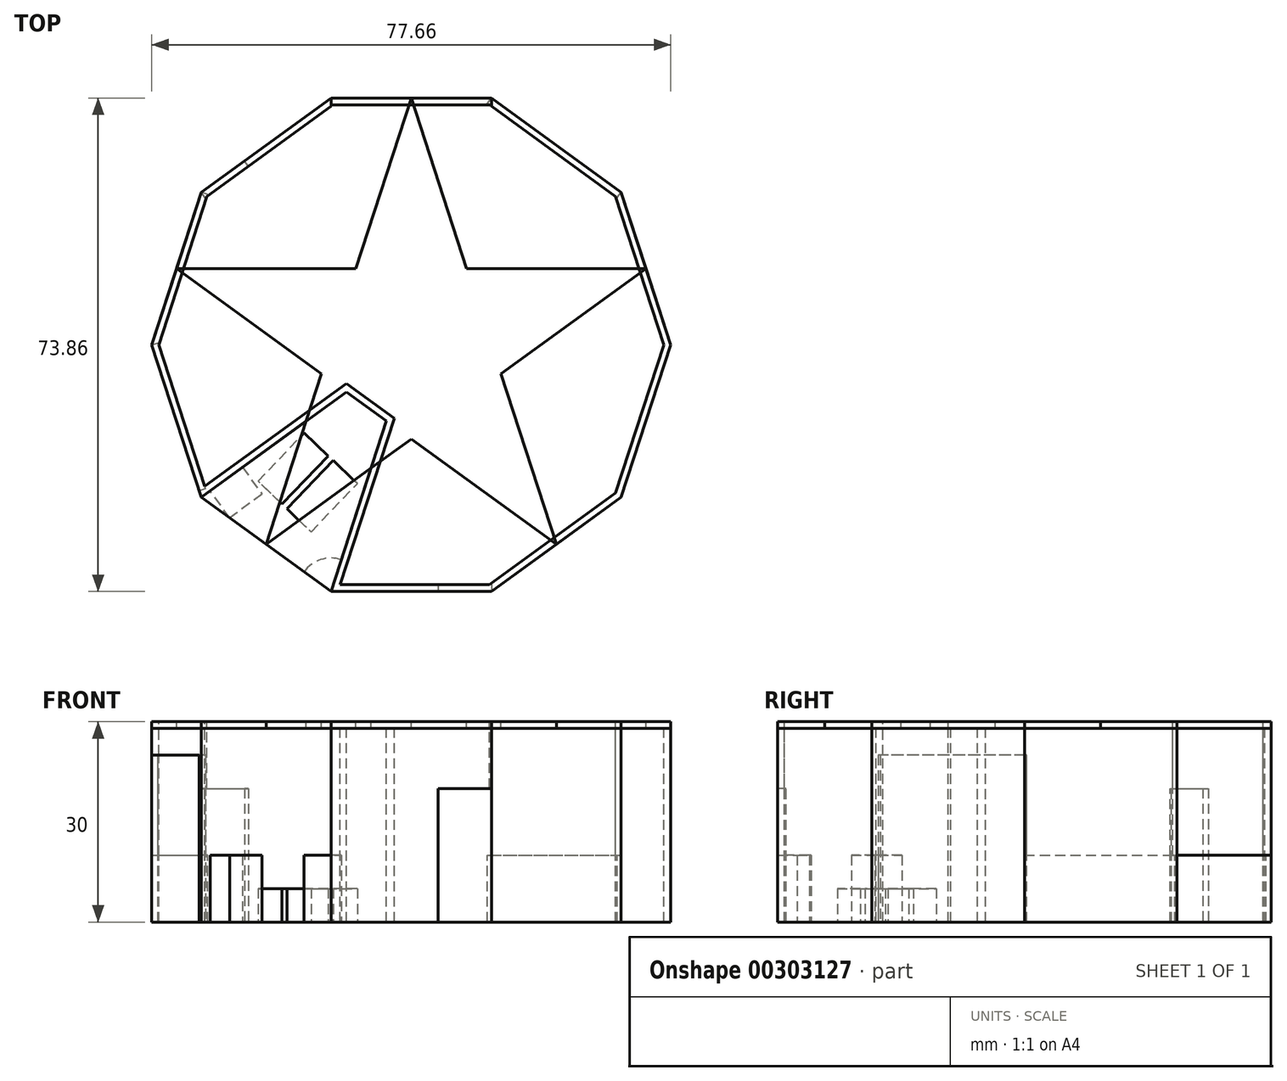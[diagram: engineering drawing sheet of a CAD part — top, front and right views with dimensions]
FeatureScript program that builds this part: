
annotation { "Feature Type Name" : "Feature", "Feature Type Description" : "" }
export const myFeature = defineFeature(function(context is Context, id is Id, definition is map)
    precondition{}
    {
        {
            var Q0;
            Q0=qCreatedBy(makeId("Top.planeOp"),FACE);
            var sketch = newSketch(context, id + "F0", { "sketchPlane" : qUnion([Q0])});
            skCircle(sketch, "E0.cCircle", {"center": v(0, 0) * mm, "radius": 38.83 * mm, "construction": true});
            skLineSegment(sketch, "E0.0", {"start": v(12, 36.93) * mm, "end": v(31.42, 22.83) * mm});
            skLineSegment(sketch, "E0.1", {"start": v(31.42, 22.83) * mm, "end": v(38.83, 0) * mm});
            skLineSegment(sketch, "E0.2", {"start": v(38.83, 0) * mm, "end": v(31.42, -22.83) * mm});
            skLineSegment(sketch, "E0.3", {"start": v(31.42, -22.83) * mm, "end": v(12, -36.93) * mm});
            skLineSegment(sketch, "E0.4", {"start": v(12, -36.93) * mm, "end": v(-12, -36.93) * mm});
            skLineSegment(sketch, "E0.5", {"start": v(-12, -36.93) * mm, "end": v(-31.42, -22.83) * mm});
            skLineSegment(sketch, "E0.6", {"start": v(-31.42, -22.83) * mm, "end": v(-38.83, 0) * mm});
            skLineSegment(sketch, "E0.7", {"start": v(-38.83, 0) * mm, "end": v(-31.42, 22.83) * mm});
            skLineSegment(sketch, "E0.8", {"start": v(-31.42, 22.83) * mm, "end": v(-12, 36.93) * mm});
            skLineSegment(sketch, "E0.9", {"start": v(-12, 36.93) * mm, "end": v(12, 36.93) * mm});
            skSolve(sketch);
        }
        {
            var Q0;
            Q0=makeQuery(id+"F0.imprint","IMPRINT",FACE,{"disambiguationData":[TD([[makeQuery(id+"F0.imprint","IMPRINT",EDGE,{"derivedFrom":sQuery(id+"F0.wireOp",EDGE,"E0.0")}),-1.0]])]});
            extrude(context, id + "F1", {"entities" : qUnion([Q0]), "oppositeDirection" : true, "depth" : 30 * mm});
        }
        {
            var Q0;
            Q0 = qSketchRegion(id + "F0", true);
            var sketch = newSketch(context, id + "F2", { "sketchPlane" : qUnion([Q0])});
            skLineSegment(sketch, "E1", {"start": v(0, 36.93) * mm, "end": v(-21.7, -29.88) * mm});
            skLineSegment(sketch, "E2", {"start": v(-21.7, -29.88) * mm, "end": v(35.12, 11.41) * mm});
            skLineSegment(sketch, "E3", {"start": v(35.12, 11.41) * mm, "end": v(-35.12, 11.41) * mm});
            skLineSegment(sketch, "E4", {"start": v(-35.12, 11.41) * mm, "end": v(21.7, -29.88) * mm});
            skLineSegment(sketch, "E5", {"start": v(21.7, -29.88) * mm, "end": v(0, 36.93) * mm});
            skSolve(sketch);
        }
        {
            var Q0;
            Q0 = qSketchRegion(id + "F0", true);
            var sketch = newSketch(context, id + "F3", { "sketchPlane" : qUnion([Q0])});
            skLineSegment(sketch, "E6", {"start": v(-31.42, -22.83) * mm, "end": v(0, 0) * mm});
            skLineSegment(sketch, "E7", {"start": v(0, 0) * mm, "end": v(-12, -36.93) * mm});
            skLineSegment(sketch, "E8", {"start": v(-12, -36.93) * mm, "end": v(-31.42, -22.83) * mm});
            skSolve(sketch);
        }
        {
            var Q0;
            Q0 = qSketchRegion(id + "F3", true);
            extrude(context, id + "F4", {"entities" : qUnion([Q0]), "operationType" : NewBodyOperationType.REMOVE, "oppositeDirection" : true, "depth" : 30 * mm});
        }
        {
            var Q0;
            Q0=makeQuery(id+"F1.opExtrude","CAP_FACE",FACE,{"disambiguationData":[OSD([sQuery(id+"F0.wireOp",EDGE,"E0.0"),sQuery(id+"F0.wireOp",EDGE,"E0.1"),sQuery(id+"F0.wireOp",EDGE,"E0.2"),sQuery(id+"F0.wireOp",EDGE,"E0.3"),sQuery(id+"F0.wireOp",EDGE,"E0.4"),sQuery(id+"F0.wireOp",EDGE,"E0.5"),sQuery(id+"F0.wireOp",EDGE,"E0.6"),sQuery(id+"F0.wireOp",EDGE,"E0.7"),sQuery(id+"F0.wireOp",EDGE,"E0.8"),sQuery(id+"F0.wireOp",EDGE,"E0.9")])],"isStart":false});
            var sketch = newSketch(context, id + "F5", { "sketchPlane" : qUnion([Q0])});
            skLineSegment(sketch, "E9", {"start": v(-31.42, 22.83) * mm, "end": v(-12, 36.93) * mm, "construction": true});
            skLineSegment(sketch, "E10", {"start": v(-30.1, 21.87) * mm, "end": v(-25.25, 18.34) * mm});
            skLineSegment(sketch, "E11", {"start": v(-25.25, 18.34) * mm, "end": v(-22.3, 22.39) * mm});
            skLineSegment(sketch, "E12", {"start": v(-22.3, 22.39) * mm, "end": v(-27.16, 25.92) * mm});
            skLineSegment(sketch, "E13", {"start": v(-27.16, 25.92) * mm, "end": v(-30.1, 21.87) * mm});
            skLineSegment(sketch, "E14", {"start": v(-31.42, 22.83) * mm, "end": v(-38.83, 0) * mm});
            skLineSegment(sketch, "E15", {"start": v(-38.83, 0) * mm, "end": v(-31.42, -22.83) * mm});
            skLineSegment(sketch, "E16", {"start": v(-31.42, -22.83) * mm, "end": v(-24.94, -27.53) * mm});
            skLineSegment(sketch, "E17", {"start": v(-12, -36.93) * mm, "end": v(12, -36.93) * mm});
            skLineSegment(sketch, "E18", {"start": v(12, -36.93) * mm, "end": v(31.42, -22.83) * mm});
            skPoint(sketch, "E19.endSnap0", {"position": v(-6, 18.47) * mm});
            skArc(sketch, "E20", {"start": v(-16.05, 34) * mm, "mid": v(-13.55, 32.18) * mm, "end": v(-10.45, 32.18) * mm});
            skLineSegment(sketch, "E21", {"start": v(12, 36.93) * mm, "end": v(4, 36.93) * mm});
            skLineSegment(sketch, "E22", {"start": v(-12, 36.93) * mm, "end": v(-16.05, 34) * mm});
            skLineSegment(sketch, "E23", {"start": v(-10.45, 32.18) * mm, "end": v(-12, 36.93) * mm});
            skLineSegment(sketch, "E24", {"start": v(-22.93, 20.41) * mm, "end": v(-16.02, 13.18) * mm});
            skLineSegment(sketch, "E25", {"start": v(-16.02, 13.18) * mm, "end": v(-12.4, 16.64) * mm});
            skLineSegment(sketch, "E26", {"start": v(-12.4, 16.64) * mm, "end": v(-19.31, 23.87) * mm});
            skLineSegment(sketch, "E27", {"start": v(-19.31, 23.87) * mm, "end": v(-22.93, 20.41) * mm});
            skLineSegment(sketch, "E28", {"start": v(-8.07, 20.78) * mm, "end": v(-11.68, 17.33) * mm});
            skLineSegment(sketch, "E29", {"start": v(-18.6, 24.56) * mm, "end": v(-14.98, 28.01) * mm});
            skLineSegment(sketch, "E30", {"start": v(-14.98, 28.01) * mm, "end": v(-8.07, 20.78) * mm});
            skLineSegment(sketch, "E31", {"start": v(-18.6, 24.56) * mm, "end": v(-11.68, 17.33) * mm});
            skLineSegment(sketch, "E32", {"start": v(-19.31, 23.87) * mm, "end": v(-18.6, 24.56) * mm, "construction": true});
            skLineSegment(sketch, "E33", {"start": v(-12.4, 16.64) * mm, "end": v(-11.68, 17.33) * mm, "construction": true});
            skSolve(sketch);
        }
        {
            var Q0;
            Q0=makeQuery(id+"F5.imprint","IMPRINT",FACE,{"disambiguationData":[TD([[makeQuery(id+"F5.imprint","IMPRINT",EDGE,{"derivedFrom":sQuery(id+"F5.wireOp",EDGE,"E20")}),1.0]])]});
            extrude(context, id + "F6", {"entities" : qUnion([Q0]), "oppositeDirection" : true, "depth" : 10 * mm});
        }
        {
            var Q0;
            Q0=makeQuery(id+"F5.imprint","IMPRINT",FACE,{"disambiguationData":[TD([[makeQuery(id+"F5.imprint","IMPRINT",EDGE,{"derivedFrom":sQuery(id+"F5.wireOp",EDGE,"E24")}),1.0]])]});
            var Q1;
            Q1=makeQuery(id+"F5.imprint","IMPRINT",FACE,{"disambiguationData":[TD([[makeQuery(id+"F5.imprint","IMPRINT",EDGE,{"derivedFrom":sQuery(id+"F5.wireOp",EDGE,"E28")}),-1.0]])]});
            extrude(context, id + "F7", {"entities" : qUnion([Q0, Q1]), "oppositeDirection" : true, "depth" : 5 * mm});
        }
        {
            var Q0;
            {var subQ1=sQuery(id+"F2.wireOp",EDGE,"E1");var subQ3=sQuery(id+"F2.wireOp",EDGE,"E4");var subQ4=makeQuery(id+"F2.imprint","INTERSECT",VERTEX,{"derivedFrom":[subQ1,subQ3]});Q0=makeQuery(id+"F2.imprint","IMPRINT",FACE,{"disambiguationData":[TD([[makeQuery(id+"F2.imprint","IMPRINT",EDGE,{"disambiguationData":[TD([[subQ4,-1.0]])],"derivedFrom":subQ3}),-1.0]])]});}
            var sketch = newSketch(context, id + "F8", { "sketchPlane" : qUnion([Q0])});
            skLineSegment(sketch, "E34", {"start": v(0, 0) * mm, "end": v(-3.7, -11.41) * mm});
            skLineSegment(sketch, "E35", {"start": v(-3.7, -11.41) * mm, "end": v(-9.7, -7.05) * mm});
            skLineSegment(sketch, "E36", {"start": v(-9.7, -7.05) * mm, "end": v(0, 0) * mm});
            skSolve(sketch);
        }
        {
            var Q0;
            Q0 = qSketchRegion(id + "F8", true);
            extrude(context, id + "F9", {"entities" : qUnion([Q0]), "operationType" : NewBodyOperationType.ADD, "oppositeDirection" : true, "depth" : 30 * mm});
        }
        {
            var Q0;
            Q0=makeQuery(id+"F9.boolean.opBoolean","MERGE",FACE,{"derivedFrom":[makeQuery(id+"FY8pf64QO3TvRso_1.boolean.opBoolean","MERGE",FACE,{"derivedFrom":[makeQuery(id+"F1.opExtrude","CAP_FACE",FACE,{"disambiguationData":[OSD([sQuery(id+"F0.wireOp",EDGE,"E0.0"),sQuery(id+"F0.wireOp",EDGE,"E0.1"),sQuery(id+"F0.wireOp",EDGE,"E0.2"),sQuery(id+"F0.wireOp",EDGE,"E0.3"),sQuery(id+"F0.wireOp",EDGE,"E0.4"),sQuery(id+"F0.wireOp",EDGE,"E0.5"),sQuery(id+"F0.wireOp",EDGE,"E0.6"),sQuery(id+"F0.wireOp",EDGE,"E0.7"),sQuery(id+"F0.wireOp",EDGE,"E0.8"),sQuery(id+"F0.wireOp",EDGE,"E0.9")])],"isStart":false}),makeQuery(id+"FY8pf64QO3TvRso_1.opExtrude","CAP_FACE",FACE,{"disambiguationData":[OSD([sQuery(id+"F5.wireOp",EDGE,"E10"),sQuery(id+"F5.wireOp",EDGE,"E11"),sQuery(id+"F5.wireOp",EDGE,"E12"),sQuery(id+"F5.wireOp",EDGE,"E13")])],"isStart":true})]}),makeQuery(id+"F9.opExtrude","CAP_FACE",FACE,{"disambiguationData":[OSD([sQuery(id+"F8.wireOp",EDGE,"E34"),sQuery(id+"F8.wireOp",EDGE,"E35"),sQuery(id+"F8.wireOp",EDGE,"E36")])],"isStart":false})]});
            var Q1;
            Q1=makeQuery(id+"F9.boolean.opBoolean","MERGE",FACE,{"derivedFrom":[makeQuery(id+"F1.opExtrude","CAP_FACE",FACE,{"disambiguationData":[OSD([sQuery(id+"F0.wireOp",EDGE,"E0.0"),sQuery(id+"F0.wireOp",EDGE,"E0.1"),sQuery(id+"F0.wireOp",EDGE,"E0.2"),sQuery(id+"F0.wireOp",EDGE,"E0.3"),sQuery(id+"F0.wireOp",EDGE,"E0.4"),sQuery(id+"F0.wireOp",EDGE,"E0.5"),sQuery(id+"F0.wireOp",EDGE,"E0.6"),sQuery(id+"F0.wireOp",EDGE,"E0.7"),sQuery(id+"F0.wireOp",EDGE,"E0.8"),sQuery(id+"F0.wireOp",EDGE,"E0.9")])],"isStart":true}),makeQuery(id+"F9.opExtrude","CAP_FACE",FACE,{"disambiguationData":[OSD([sQuery(id+"F8.wireOp",EDGE,"E34"),sQuery(id+"F8.wireOp",EDGE,"E35"),sQuery(id+"F8.wireOp",EDGE,"E36")])],"isStart":true})]});
            shell(context, id + "F10", {"entities" : qUnion([Q0, Q1]), "thickness" : 1 * mm});
        }
        {
            var Q0;
            Q0=makeQuery(id+"F1.opExtrude","SWEPT_FACE",FACE,{"disambiguationData":[OSD([sQuery(id+"F0.wireOp",EDGE,"E0.4")])]});
            var sketch = newSketch(context, id + "F11", { "sketchPlane" : qUnion([Q0])});
            skLineSegment(sketch, "E37", {"start": v(4, -30) * mm, "end": v(4, -10) * mm});
            skLineSegment(sketch, "E38", {"start": v(4, -10) * mm, "end": v(12, -10) * mm});
            skLineSegment(sketch, "E39", {"start": v(12, -10) * mm, "end": v(12, -30) * mm});
            skLineSegment(sketch, "E40", {"start": v(12, -30) * mm, "end": v(4, -30) * mm});
            skSolve(sketch);
        }
        {
            var Q0;
            Q0=makeQuery(id+"F11.imprint","IMPRINT",FACE,{"disambiguationData":[TD([[makeQuery(id+"F11.imprint","IMPRINT",EDGE,{"derivedFrom":sQuery(id+"F11.wireOp",EDGE,"E37")}),-1.0]])]});
            extrude(context, id + "F12", {"entities" : qUnion([Q0]), "operationType" : NewBodyOperationType.REMOVE, "endBound" : BoundingType.UP_TO_NEXT, "oppositeDirection" : true, "depth" : 25 * mm});
        }
        {
            var Q0;
            Q0=makeQuery(id+"F1.opExtrude","SWEPT_FACE",FACE,{"disambiguationData":[OSD([sQuery(id+"F0.wireOp",EDGE,"E0.7")])]});
            var sketch = newSketch(context, id + "F13", { "sketchPlane" : qUnion([Q0])});
            skLineSegment(sketch, "E41", {"start": v(-12, -30) * mm, "end": v(12, -30) * mm});
            skLineSegment(sketch, "E42", {"start": v(12, -30) * mm, "end": v(12, -20) * mm});
            skLineSegment(sketch, "E43", {"start": v(12, -20) * mm, "end": v(-12, -20) * mm});
            skLineSegment(sketch, "E44", {"start": v(-12, -20) * mm, "end": v(-12, -30) * mm});
            skSolve(sketch);
        }
        {
            var Q0;
            Q0=makeQuery(id+"F13.imprint","IMPRINT",FACE,{"disambiguationData":[TD([[makeQuery(id+"F13.imprint","IMPRINT",EDGE,{"derivedFrom":sQuery(id+"F13.wireOp",EDGE,"E41")}),-1.0]])]});
            extrude(context, id + "F14", {"entities" : qUnion([Q0]), "operationType" : NewBodyOperationType.REMOVE, "endBound" : BoundingType.UP_TO_NEXT, "oppositeDirection" : true, "depth" : 25 * mm});
        }
        {
            var Q0;
            Q0=makeQuery(id+"F13.imprint","IMPRINT",FACE,{"disambiguationData":[TD([[makeQuery(id+"F13.imprint","IMPRINT",EDGE,{"derivedFrom":sQuery(id+"F13.wireOp",EDGE,"E41")}),-1.0]])]});
            extrude(context, id + "F15", {"entities" : qUnion([Q0]), "oppositeDirection" : true, "depth" : 1 * mm});
        }
        {
            var Q0;
            Q0=makeQuery(id+"F1.opExtrude","SWEPT_FACE",FACE,{"disambiguationData":[OSD([sQuery(id+"F0.wireOp",EDGE,"E0.8")])]});
            var sketch = newSketch(context, id + "F16", { "sketchPlane" : qUnion([Q0])});
            skLineSegment(sketch, "E45", {"start": v(12, -30) * mm, "end": v(12, -10) * mm});
            skLineSegment(sketch, "E46", {"start": v(12, -10) * mm, "end": v(4, -10) * mm});
            skLineSegment(sketch, "E47", {"start": v(4, -10) * mm, "end": v(4, -30) * mm});
            skLineSegment(sketch, "E48", {"start": v(4, -30) * mm, "end": v(12, -30) * mm});
            skSolve(sketch);
        }
        {
            var Q0;
            {var subQ0=sQuery(id+"F16.wireOp",EDGE,"E46");Q0=makeQuery(id+"F16.imprint","IMPRINT",FACE,{"disambiguationData":[TD([[makeQuery(id+"F16.imprint","IMPRINT",EDGE,{"derivedFrom":subQ0}),1.0]])]});}
            extrude(context, id + "F17", {"entities" : qUnion([Q0]), "operationType" : NewBodyOperationType.REMOVE, "endBound" : BoundingType.UP_TO_NEXT, "oppositeDirection" : true, "depth" : 25 * mm});
        }
        {
            var Q0;
            {var subQ0=sQuery(id+"F16.wireOp",EDGE,"E46");Q0=makeQuery(id+"F16.imprint","IMPRINT",FACE,{"disambiguationData":[TD([[makeQuery(id+"F16.imprint","IMPRINT",EDGE,{"derivedFrom":subQ0}),1.0]])]});}
            extrude(context, id + "F18", {"entities" : qUnion([Q0]), "oppositeDirection" : true, "depth" : 1 * mm});
        }
        {
            var Q0;
            Q0=makeQuery(id+"F1.opExtrude","SWEPT_FACE",FACE,{"disambiguationData":[OSD([sQuery(id+"F0.wireOp",EDGE,"E0.9")])]});
            var sketch = newSketch(context, id + "F19", { "sketchPlane" : qUnion([Q0])});
            skLineSegment(sketch, "E49", {"start": v(-12, -30) * mm, "end": v(12, -30) * mm});
            skLineSegment(sketch, "E50", {"start": v(12, -30) * mm, "end": v(12, 0) * mm});
            skLineSegment(sketch, "E51", {"start": v(12, 0) * mm, "end": v(-12, 0) * mm});
            skLineSegment(sketch, "E52", {"start": v(-12, 0) * mm, "end": v(-12, -30) * mm});
            skSolve(sketch);
        }
        {
            var Q0;
            Q0 = qSketchRegion(id + "F19", true);
            extrude(context, id + "F20", {"entities" : qUnion([Q0]), "operationType" : NewBodyOperationType.REMOVE, "endBound" : BoundingType.UP_TO_NEXT, "oppositeDirection" : true, "depth" : 25 * mm});
        }
        {
            var Q0;
            Q0=makeQuery(id+"F19.imprint","IMPRINT",FACE,{"disambiguationData":[TD([[makeQuery(id+"F19.imprint","IMPRINT",EDGE,{"derivedFrom":sQuery(id+"F19.wireOp",EDGE,"E49")}),-1.0]])]});
            extrude(context, id + "F21", {"entities" : qUnion([Q0]), "oppositeDirection" : true, "depth" : 1 * mm});
        }
        {
            var Q0;
            Q0=makeQuery(id+"F1.opExtrude","SWEPT_FACE",FACE,{"disambiguationData":[OSD([sQuery(id+"F0.wireOp",EDGE,"E0.0")])]});
            var sketch = newSketch(context, id + "F22", { "sketchPlane" : qUnion([Q0])});
            skLineSegment(sketch, "E53", {"start": v(-12, -30) * mm, "end": v(12, -30) * mm});
            skLineSegment(sketch, "E54", {"start": v(12, -30) * mm, "end": v(12, -20) * mm});
            skLineSegment(sketch, "E55", {"start": v(12, -20) * mm, "end": v(-12, -20) * mm});
            skLineSegment(sketch, "E56", {"start": v(-12, -20) * mm, "end": v(-12, -30) * mm});
            skSolve(sketch);
        }
        {
            var Q0;
            Q0=makeQuery(id+"F22.imprint","IMPRINT",FACE,{"disambiguationData":[TD([[makeQuery(id+"F22.imprint","IMPRINT",EDGE,{"derivedFrom":sQuery(id+"F22.wireOp",EDGE,"E53")}),-1.0]])]});
            extrude(context, id + "F23", {"entities" : qUnion([Q0]), "operationType" : NewBodyOperationType.REMOVE, "endBound" : BoundingType.UP_TO_NEXT, "oppositeDirection" : true, "depth" : 25 * mm});
        }
        {
            var Q0;
            Q0 = qSketchRegion(id + "F22", true);
            extrude(context, id + "F24", {"entities" : qUnion([Q0]), "oppositeDirection" : true, "depth" : 1 * mm});
        }
        {
            var Q0;
            Q0=makeQuery(id+"F11.imprint","IMPRINT",FACE,{"disambiguationData":[TD([[makeQuery(id+"F11.imprint","IMPRINT",EDGE,{"derivedFrom":sQuery(id+"F11.wireOp",EDGE,"E37")}),-1.0]])]});
            extrude(context, id + "F25", {"entities" : qUnion([Q0]), "oppositeDirection" : true, "depth" : 1 * mm});
        }
        {
            var Q0;
            {var subQ0=makeQuery(id+"F0.imprint","IMPRINT",EDGE,{"derivedFrom":sQuery(id+"F0.wireOp",EDGE,"E0.8")});Q0=makeQuery(id+"F2.imprint","IMPRINT",FACE,{"disambiguationData":[TD([[makeQuery(id+"F2.imprint","IMPRINT",EDGE,{"derivedFrom":subQ0}),-1.0]])]});}
            var Q1;
            {var subQ1=makeQuery(id+"F0.imprint","IMPRINT",EDGE,{"derivedFrom":sQuery(id+"F0.wireOp",EDGE,"E0.0")});Q1=makeQuery(id+"F2.imprint","IMPRINT",FACE,{"disambiguationData":[TD([[makeQuery(id+"F2.imprint","IMPRINT",EDGE,{"derivedFrom":subQ1}),-1.0]])]});}
            var Q2;
            {var subQ0=makeQuery(id+"F0.imprint","IMPRINT",EDGE,{"derivedFrom":sQuery(id+"F0.wireOp",EDGE,"E0.2")});Q2=makeQuery(id+"F2.imprint","IMPRINT",FACE,{"disambiguationData":[TD([[makeQuery(id+"F2.imprint","IMPRINT",EDGE,{"derivedFrom":subQ0}),-1.0]])]});}
            extrude(context, id + "F26", {"entities" : qUnion([Q0, Q1, Q2]), "oppositeDirection" : true, "depth" : 1 * mm});
        }
        {
            var Q0;
            {var subQ0=makeQuery(id+"F0.imprint","IMPRINT",EDGE,{"derivedFrom":sQuery(id+"F0.wireOp",EDGE,"E0.6")});Q0=makeQuery(id+"F2.imprint","IMPRINT",FACE,{"disambiguationData":[TD([[makeQuery(id+"F2.imprint","IMPRINT",EDGE,{"derivedFrom":subQ0}),-1.0]])]});}
            var sketch = newSketch(context, id + "F27", { "sketchPlane" : qUnion([Q0])});
            skLineSegment(sketch, "E57", {"start": v(-31.42, -22.83) * mm, "end": v(-38.83, 0) * mm});
            skLineSegment(sketch, "E58", {"start": v(-38.83, 0) * mm, "end": v(-35.12, 11.41) * mm});
            skLineSegment(sketch, "E59", {"start": v(-35.12, 11.41) * mm, "end": v(-13.42, -4.36) * mm});
            skLineSegment(sketch, "E60", {"start": v(-13.42, -4.36) * mm, "end": v(-15.7, -11.41) * mm});
            skLineSegment(sketch, "E61", {"start": v(-15.7, -11.41) * mm, "end": v(-31.42, -22.83) * mm});
            skLineSegment(sketch, "E62", {"start": v(-12, -36.93) * mm, "end": v(-6, -18.47) * mm});
            skLineSegment(sketch, "E63", {"start": v(-6, -18.47) * mm, "end": v(0, -14.1) * mm});
            skLineSegment(sketch, "E64", {"start": v(0, -14.1) * mm, "end": v(21.7, -29.88) * mm});
            skLineSegment(sketch, "E65", {"start": v(21.7, -29.88) * mm, "end": v(12, -36.93) * mm});
            skLineSegment(sketch, "E66", {"start": v(12, -36.93) * mm, "end": v(-12, -36.93) * mm});
            skSolve(sketch);
        }
        {
            var Q0;
            Q0=makeQuery(id+"F27.imprint","IMPRINT",FACE,{"disambiguationData":[TD([[makeQuery(id+"F27.imprint","IMPRINT",EDGE,{"derivedFrom":sQuery(id+"F27.wireOp",EDGE,"E57")}),-1.0]])]});
            var Q1;
            Q1=makeQuery(id+"F27.imprint","IMPRINT",FACE,{"disambiguationData":[TD([[makeQuery(id+"F27.imprint","IMPRINT",EDGE,{"derivedFrom":sQuery(id+"F27.wireOp",EDGE,"E62")}),-1.0]])]});
            extrude(context, id + "F28", {"entities" : qUnion([Q0, Q1]), "oppositeDirection" : true, "depth" : 1 * mm});
        }
        {
            var Q0;
            Q0=makeQuery(id+"F1.opExtrude","SWEPT_FACE",FACE,{"disambiguationData":[OSD([sQuery(id+"F0.wireOp",EDGE,"E0.6")])]});
            var sketch = newSketch(context, id + "F29", { "sketchPlane" : qUnion([Q0])});
            skLineSegment(sketch, "E67", {"start": v(-12, -30) * mm, "end": v(-12, -5) * mm});
            skLineSegment(sketch, "E68", {"start": v(-12, -5) * mm, "end": v(11, -5) * mm});
            skLineSegment(sketch, "E69", {"start": v(11, -5) * mm, "end": v(11, -30) * mm});
            skLineSegment(sketch, "E70", {"start": v(11, -30) * mm, "end": v(-12, -30) * mm});
            skSolve(sketch);
        }
        {
            var Q0;
            {var subQ0=sQuery(id+"F29.wireOp",EDGE,"E68");Q0=makeQuery(id+"F29.imprint","IMPRINT",FACE,{"disambiguationData":[TD([[makeQuery(id+"F29.imprint","IMPRINT",EDGE,{"derivedFrom":subQ0}),-1.0]])]});}
            extrude(context, id + "F30", {"entities" : qUnion([Q0]), "operationType" : NewBodyOperationType.REMOVE, "oppositeDirection" : true, "depth" : 1 * mm});
        }
        {
            var Q0;
            Q0 = qSketchRegion(id + "F29", true);
            extrude(context, id + "F31", {"entities" : qUnion([Q0]), "oppositeDirection" : true, "depth" : 1 * mm});
        }
        {
            var Q0;
            {var subQ0=makeQuery(id+"F0.imprint","IMPRINT",EDGE,{"derivedFrom":sQuery(id+"F0.wireOp",EDGE,"E0.6")});Q0=makeQuery(id+"F2.imprint","IMPRINT",FACE,{"disambiguationData":[TD([[makeQuery(id+"F2.imprint","IMPRINT",EDGE,{"derivedFrom":subQ0}),-1.0]])]});}
            var sketch = newSketch(context, id + "F32", { "sketchPlane" : qUnion([Q0])});
            skLineSegment(sketch, "E71", {"start": v(-31.42, -22.83) * mm, "end": v(-21.7, -29.88) * mm});
            skLineSegment(sketch, "E72", {"start": v(-21.7, -29.88) * mm, "end": v(-15.7, -11.41) * mm});
            skLineSegment(sketch, "E73", {"start": v(-15.7, -11.41) * mm, "end": v(-31.42, -22.83) * mm});
            skLineSegment(sketch, "E74", {"start": v(-21.7, -29.88) * mm, "end": v(-12, -36.93) * mm});
            skLineSegment(sketch, "E75", {"start": v(-12, -36.93) * mm, "end": v(-6, -18.47) * mm});
            skLineSegment(sketch, "E76", {"start": v(-6, -18.47) * mm, "end": v(-21.7, -29.88) * mm});
            skLineSegment(sketch, "E77", {"start": v(-31.42, -22.83) * mm, "end": v(-12, -36.93) * mm, "construction": true});
            skSolve(sketch);
        }
        {
            var Q0;
            Q0=makeQuery(id+"F32.imprint","IMPRINT",FACE,{"disambiguationData":[TD([[makeQuery(id+"F32.imprint","IMPRINT",EDGE,{"derivedFrom":sQuery(id+"F32.wireOp",EDGE,"E71")}),-1.0]])]});
            var Q1;
            Q1=makeQuery(id+"F32.imprint","IMPRINT",FACE,{"disambiguationData":[TD([[makeQuery(id+"F32.imprint","IMPRINT",EDGE,{"derivedFrom":sQuery(id+"F32.wireOp",EDGE,"E74")}),1.0]])]});
            extrude(context, id + "F33", {"entities" : qUnion([Q0, Q1]), "oppositeDirection" : true, "depth" : 1 * mm});
        }
        {
            var Q0;
            Q0=makeQuery(id+"F5.imprint","IMPRINT",FACE,{"disambiguationData":[TD([[makeQuery(id+"F5.imprint","IMPRINT",EDGE,{"derivedFrom":sQuery(id+"F5.wireOp",EDGE,"E10")}),1.0]])]});
            extrude(context, id + "F34", {"entities" : qUnion([Q0]), "oppositeDirection" : true, "depth" : 10 * mm});
        }
    });
